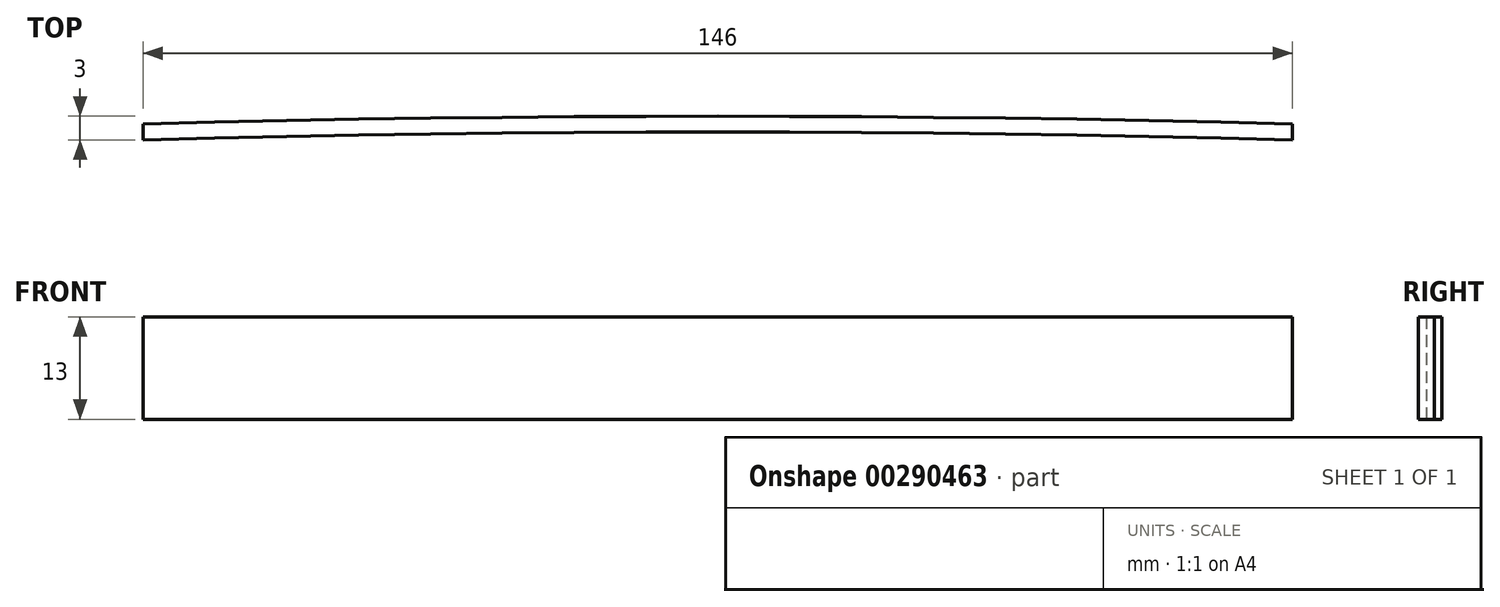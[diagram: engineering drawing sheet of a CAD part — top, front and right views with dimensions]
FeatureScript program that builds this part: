
annotation { "Feature Type Name" : "Feature", "Feature Type Description" : "" }
export const myFeature = defineFeature(function(context is Context, id is Id, definition is map)
    precondition{}
    {
        {
            var Q0;
            Q0=qCreatedBy(makeId("Top.planeOp"),FACE);
            var sketch = newSketch(context, id + "F0", { "sketchPlane" : qUnion([Q0])});
            skArc(sketch, "E0", {"start": v(72.46, 6.93) * mm, "mid": v(-0.54, 7.93) * mm, "end": v(-73.54, 6.93) * mm});
            skLineSegment(sketch, "E1", {"start": v(-73.54, 6.93) * mm, "end": v(-73.54, 4.93) * mm});
            skLineSegment(sketch, "E2", {"start": v(72.46, 6.93) * mm, "end": v(72.46, 4.93) * mm});
            skArc(sketch, "E3", {"start": v(72.46, 4.93) * mm, "mid": v(-0.54, 5.93) * mm, "end": v(-73.54, 4.93) * mm});
            skLineSegment(sketch, "E4", {"start": v(-73.54, 4.93) * mm, "end": v(72.46, 4.93) * mm, "construction": true});
            skSolve(sketch);
        }
        {
            var Q0;
            Q0=qSketchRegion(id+"F0",true);
            extrude(context, id + "F1", {"entities" : qUnion([Q0]), "depth" : 13 * mm});
        }
    });
